FCSTD DOCUMENT  (FreeCAD 0.16RUnknown)
Label: Art1BodyP3B_backup
License: CreativeCommons Attribution-ShareAlike
LicenseURL: http://creativecommons.org/licenses/by-sa/4.0/
objects: Sketcher::SketchObject×5, Mesh::Feature×2, PartDesign::Pocket×2, PartDesign::Revolution×1, PartDesign::Pad×1, Part::Cut×1
note: 14 computed .brp shape members not serialized (recipe doc carries the construction recipe); baked Part::Feature solids carry a one-line shape summary decoded from their .brp

FEATURE [Mesh::Feature] Art1Body_P3A
  Placement = pos=(0,0,0) rot=(1,0,0;1.5708rad)
FEATURE [Mesh::Feature] Art1Body_P3B
FEATURE [Sketcher::SketchObject] Sketch
  sketch-geometry (4):
    g0: ArcOfCircle CenterX=0 CenterY=12 CenterZ=0 NormalX=0 NormalY=0 NormalZ=1 Radius=61 StartAngle=3.33961 EndAngle=6.08517
    g1: ArcOfCircle CenterX=0 CenterY=12 CenterZ=0 NormalX=0 NormalY=0 NormalZ=1 Radius=66 StartAngle=3.32443 EndAngle=6.10035
    g2: LineSegment StartX=-64.8999 StartY=0 StartZ=0 EndX=-59.808 EndY=0 EndZ=0
    g3: LineSegment StartX=59.808 StartY=0 StartZ=0 EndX=64.8999 EndY=0 EndZ=0
  constraints (16):
    c: PointOnObject(g0,g-2)
    c: PointOnObject(g0,g-1)
    c: PointOnObject(g0,g-1)
    c: PointOnObject(g1,g-2)
    c: PointOnObject(g1,g-1)
    c: PointOnObject(g1,g-1)
    c: Radius(g0) = 61
    c: DistanceY(g1) = 12
    c: Radius(g1) = 66
    c: Coincident(g0,g1)
    c: Coincident(g2,g1)
    c: Horizontal(g2)
    c: Coincident(g3,g0)
    c: Horizontal(g3)
    c: Coincident(g1,g3)
    c: Coincident(g0,g2)
FEATURE [PartDesign::Revolution] Revolution
  Angle = 90
  Axis = (1,0,0)
  Base = (0,0,0)
  ReferenceAxis = -> Sketch [H_Axis]
  Reversed = true
  Sketch = -> Sketch
FEATURE [Sketcher::SketchObject] Sketch001
  sketch-geometry (4):
    g0: ArcOfCircle CenterX=0 CenterY=12 CenterZ=0 NormalX=0 NormalY=0 NormalZ=1 Radius=50 StartAngle=4.10152 EndAngle=5.32325
    g1: ArcOfCircle CenterX=20.7294 CenterY=70.272 CenterZ=0 NormalX=0 NormalY=0 NormalZ=1 Radius=110.85 StartAngle=3.82823 EndAngle=4.25041
    g2: ArcOfCircle CenterX=-48.6951 CenterY=105.349 CenterZ=0 NormalX=0 NormalY=0 NormalZ=1 Radius=155 StartAngle=5.23505 EndAngle=5.53587
    g3: LineSegment StartX=-65 StartY=0 StartZ=0 EndX=65 EndY=0 EndZ=0
  constraints (15):
    c: PointOnObject(g0,g-2)
    c: Radius(g0) = 50
    c: DistanceY(g0) = 12
    c: Symmetric(g0,g0,g-2)
    c: Angle(g0) = 1.22173
    c: Coincident(g0,g1)
    c: PointOnObject(g1,g-1)
    c: Coincident(g0,g2)
    c: PointOnObject(g2,g-1)
    c: DistanceX(g2) = 65
    c: Radius(g2) = 155
    c: Symmetric(g1,g2,g-2)
    c: PointOnObject(g3,g-1)
    c: PointOnObject(g3,g-1)
    c: Coincident(g1,g3)
FEATURE [PartDesign::Pad] Pad
  Length = 55
  Length2 = 100
  Sketch = -> Sketch001
  Type = 0
FEATURE [Part::Cut] Cut  label="base"
  Base = -> Revolution
  Tool = -> Pad
FEATURE [Sketcher::SketchObject] Sketch002
  Placement = pos=(0,0,0) rot=(1,0,0;3.14159rad)
  Support = -> Cut [Face2]
  sketch-geometry (3):
    g0: Circle CenterX=15.029 CenterY=50.0941 CenterZ=0 NormalX=0 NormalY=0 NormalZ=1 Radius=1
    g1: Circle CenterX=-15.029 CenterY=50.0941 CenterZ=0 NormalX=0 NormalY=0 NormalZ=1 Radius=1
    g2: LineSegment [constr] StartX=0 StartY=0 StartZ=0 EndX=15.029 EndY=50.0941 EndZ=0
  constraints (7):
    c: Coincident(g2,g-1)
    c: Coincident(g2,g0)
    c: Angle(g2,g-2) = 0.29147
    c: Distance(g2) = 52.3
    c: Radius(g0) = 1
    c: Equal(g1,g0)
    c: Symmetric(g1,g0,g-2)
FEATURE [PartDesign::Pocket] Pocket  label="holesScrews"
  Length = 5
  Sketch = -> Sketch002
  Type = 1
FEATURE [Sketcher::SketchObject] Sketch003
  Placement = pos=(0,0,0) rot=(0,0.707107,0.707107;3.14159rad)
  Support = -> Revolution [Face4]
  sketch-geometry (20):
    g0: LineSegment StartX=-32.5 StartY=0 StartZ=0 EndX=-27.5 EndY=0 EndZ=0
    g1: LineSegment StartX=-27.5 StartY=0 StartZ=0 EndX=-27.5 EndY=17.5 EndZ=0
    g2: LineSegment StartX=-32.5 StartY=17.5 StartZ=0 EndX=-32.5 EndY=0 EndZ=0
    g3: ArcOfCircle CenterX=-30 CenterY=17.5 CenterZ=0 NormalX=0 NormalY=0 NormalZ=1 Radius=2.5 StartAngle=6.28319 EndAngle=9.42478
    g4: LineSegment StartX=27.5 StartY=0 StartZ=0 EndX=27.5 EndY=17.5 EndZ=0
    g5: LineSegment StartX=27.5 StartY=0 StartZ=0 EndX=32.5 EndY=0 EndZ=0
    g6: LineSegment StartX=32.5 StartY=0 StartZ=0 EndX=32.5 EndY=17.5 EndZ=0
    g7: ArcOfCircle CenterX=30 CenterY=17.5 CenterZ=0 NormalX=0 NormalY=0 NormalZ=1 Radius=2.5 StartAngle=3.87425e-07 EndAngle=3.14159
    g8: LineSegment StartX=-2.5 StartY=17.5 StartZ=0 EndX=-2.5 EndY=0 EndZ=0
    g9: LineSegment StartX=-2.5 StartY=0 StartZ=0 EndX=2.5 EndY=0 EndZ=0
    g10: LineSegment StartX=2.5 StartY=0 StartZ=0 EndX=2.5 EndY=17.5 EndZ=0
    g11: ArcOfCircle CenterX=0 CenterY=17.5 CenterZ=0 NormalX=0 NormalY=0 NormalZ=1 Radius=2.5 StartAngle=6.28319 EndAngle=9.42478
    g12: LineSegment StartX=12.5 StartY=6 StartZ=0 EndX=17.5 EndY=6 EndZ=0
    g13: LineSegment StartX=17.5 StartY=6 StartZ=0 EndX=17.5 EndY=4 EndZ=0
    g14: LineSegment StartX=17.5 StartY=4 StartZ=0 EndX=12.5 EndY=4 EndZ=0
    g15: LineSegment StartX=12.5 StartY=4 StartZ=0 EndX=12.5 EndY=6 EndZ=0
    g16: LineSegment StartX=-17.5 StartY=6 StartZ=0 EndX=-12.5 EndY=6 EndZ=0
    g17: LineSegment StartX=-12.5 StartY=6 StartZ=0 EndX=-12.5 EndY=4 EndZ=0
    g18: LineSegment StartX=-12.5 StartY=4 StartZ=0 EndX=-17.5 EndY=4 EndZ=0
    g19: LineSegment StartX=-17.5 StartY=4 StartZ=0 EndX=-17.5 EndY=6 EndZ=0
  constraints (63):
    c: Coincident(g0,g1)
    c: Coincident(g2,g0)
    c: Horizontal(g0)
    c: Vertical(g1)
    c: Vertical(g2)
    c: PointOnObject(g0,g-1)
    c: PointOnObject(g3,g2)
    c: Coincident(g3,g1)
    c: Coincident(g2,g3)
    c: PointOnObject(g4,g-1)
    c: Vertical(g4)
    c: Coincident(g4,g5)
    c: Horizontal(g5)
    c: Coincident(g5,g6)
    c: Vertical(g6)
    c: Coincident(g7,g4)
    c: Coincident(g7,g6)
    c: Tangent(g7,g4)
    c: Tangent(g7,g6)
    c: Tangent(g3,g2)
    c: Tangent(g3,g1)
    c: Vertical(g8)
    c: Coincident(g8,g9)
    c: PointOnObject(g9,g-1)
    c: Coincident(g9,g10)
    c: Vertical(g10)
    c: Coincident(g11,g8)
    c: Coincident(g11,g10)
    c: PointOnObject(g8,g-1)
    c: Tangent(g8,g11,g8) = -1.5708
    c: Tangent(g11,g10)
    c: Equal(g3,g11)
    c: Equal(g11,g7)
    c: Radius(g11) = 2.5
    c: Symmetric(g8,g9,g-2)
    c: Symmetric(g0,g4,g-2)
    c: DistanceY(g10,g10) = 17.5
    c: Equal(g1,g10)
    c: Equal(g10,g6)
    c: DistanceX(g4) = 27.5
    c: Coincident(g12,g13)
    c: Coincident(g13,g14)
    c: Coincident(g14,g15)
    c: Coincident(g15,g12)
    c: Horizontal(g12)
    c: Horizontal(g14)
    c: Vertical(g13)
    c: Vertical(g15)
    c: Coincident(g16,g17)
    c: Coincident(g17,g18)
    c: Coincident(g18,g19)
    c: Coincident(g19,g16)
    c: Horizontal(g16)
    c: Horizontal(g18)
    c: Vertical(g17)
    c: Vertical(g19)
    c: Equal(g12,g16)
    c: Equal(g15,g17)
    c: Symmetric(g14,g17,g-2)
    c: DistanceX(g14) = 12.5
    c: DistanceY(g14) = 4
    c: DistanceY(g13,g13) = 2
    c: DistanceX(g12,g12) = 5
FEATURE [PartDesign::Pocket] Pocket001
  Length = 5
  Sketch = -> Sketch003
  Type = 1
FEATURE [Sketcher::SketchObject] Sketch004
  sketch-geometry (4):
    g0: ArcOfCircle CenterX=0 CenterY=12 CenterZ=0 NormalX=0 NormalY=0 NormalZ=1 Radius=50 StartAngle=4.10152 EndAngle=5.32325
    g1: ArcOfCircle CenterX=20.7294 CenterY=70.272 CenterZ=0 NormalX=0 NormalY=0 NormalZ=1 Radius=110.85 StartAngle=3.82823 EndAngle=4.25041
    g2: ArcOfCircle CenterX=-48.6951 CenterY=105.349 CenterZ=0 NormalX=0 NormalY=0 NormalZ=1 Radius=155 StartAngle=5.23505 EndAngle=5.53587
    g3: LineSegment StartX=-65 StartY=0 StartZ=0 EndX=65 EndY=0 EndZ=0
  constraints (15):
    c: PointOnObject(g0,g-2)
    c: Radius(g0) = 50
    c: DistanceY(g0) = 12
    c: Symmetric(g0,g0,g-2)
    c: Angle(g0) = 1.22173
    c: Coincident(g0,g1)
    c: PointOnObject(g1,g-1)
    c: Coincident(g0,g2)
    c: PointOnObject(g2,g-1)
    c: DistanceX(g2) = 65
    c: Radius(g2) = 155
    c: Symmetric(g1,g2,g-2)
    c: PointOnObject(g3,g-1)
    c: PointOnObject(g3,g-1)
    c: Coincident(g1,g3)
